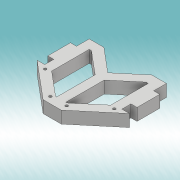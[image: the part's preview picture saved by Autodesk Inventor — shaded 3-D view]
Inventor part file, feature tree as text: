
AUTODESK INVENTOR PART (.ipt)
format: ipt  version: 2019 (Build 230136000, 136)  size: 153,088 bytes
history: native  units: mm
features: extrude x1
ambient origin geometry x8: Origin, YZ Plane, XZ Plane, XY Plane, X Axis, Y Axis, Z Axis, Center Point
bodies: Solid1 (feature_tree)
feature tree (1):
  extrude  "Extrusion1"  Depth=5.0135mm
